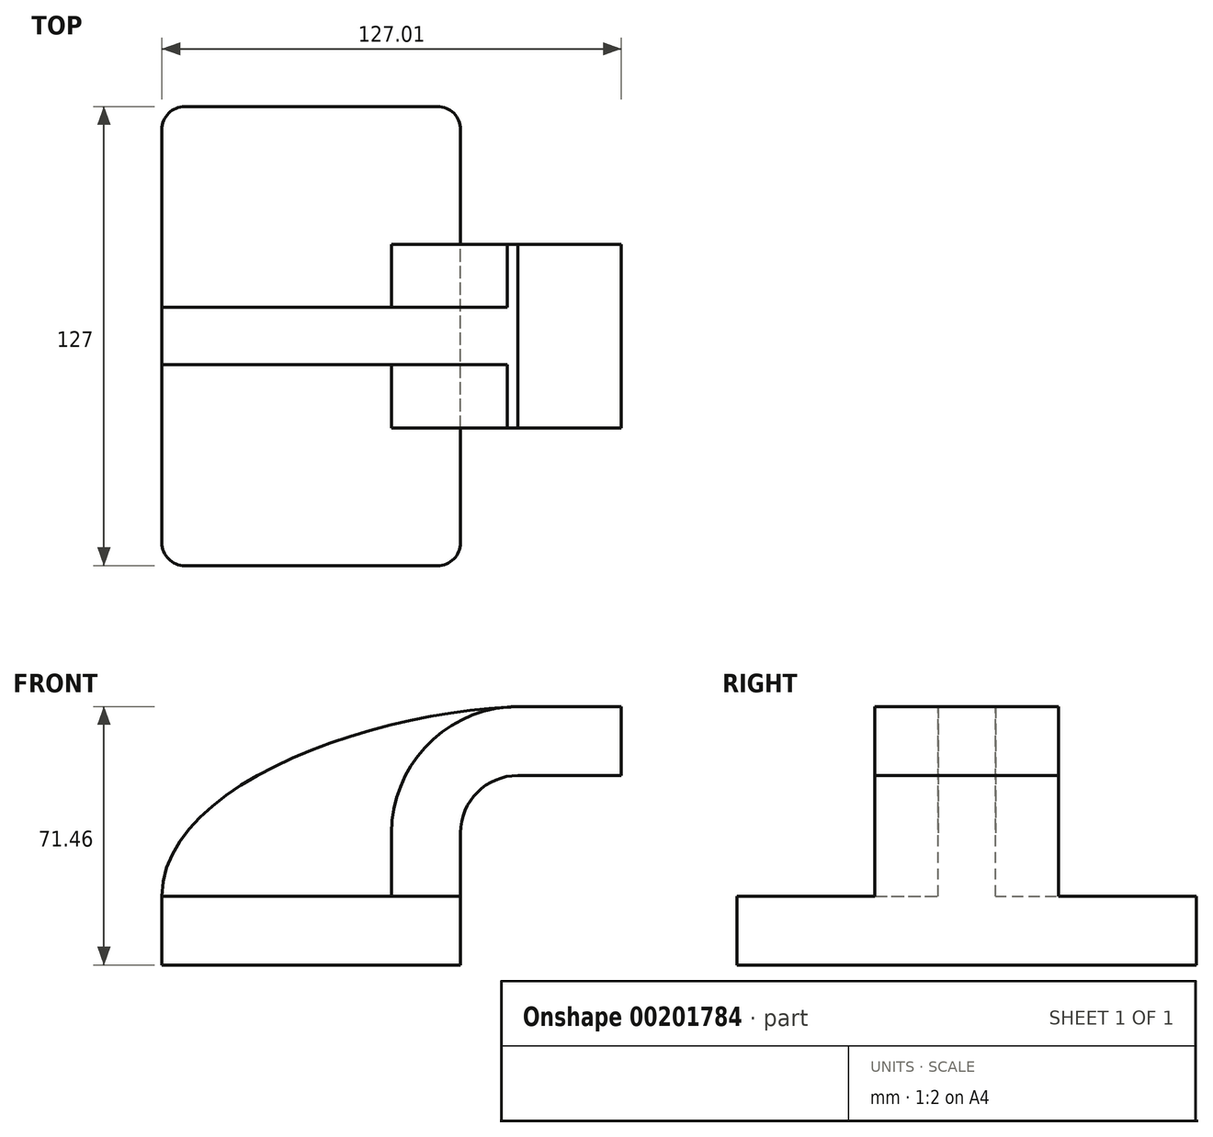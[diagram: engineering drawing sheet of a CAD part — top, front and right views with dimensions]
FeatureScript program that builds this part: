
annotation { "Feature Type Name" : "Feature", "Feature Type Description" : "" }
export const myFeature = defineFeature(function(context is Context, id is Id, definition is map)
    precondition{}
    {
        {
            var Q0;
            Q0=qCreatedBy(makeId("Front.planeOp"),FACE);
            var sketch = newSketch(context, id + "F0", { "sketchPlane" : qUnion([Q0])});
            skLineSegment(sketch, "E0.bottom", {"start": v(41.27, 9.53) * mm, "end": v(-41.28, 9.53) * mm});
            skLineSegment(sketch, "E0.top", {"start": v(41.28, -9.52) * mm, "end": v(-41.27, -9.52) * mm});
            skLineSegment(sketch, "E0.left", {"start": v(41.28, 9.53) * mm, "end": v(41.28, -9.52) * mm});
            skLineSegment(sketch, "E0.right", {"start": v(-41.28, 9.53) * mm, "end": v(-41.28, -9.52) * mm});
            skPoint(sketch, "E0.middle", {"position": v(0, 0) * mm});
            skLineSegment(sketch, "E1.bottom", {"start": v(60.32, 66.68) * mm, "end": v(111.12, 66.68) * mm});
            skLineSegment(sketch, "E1.top", {"start": v(60.32, 38.1) * mm, "end": v(111.12, 38.1) * mm});
            skLineSegment(sketch, "E1.left", {"start": v(60.32, 66.68) * mm, "end": v(60.32, 38.1) * mm});
            skLineSegment(sketch, "E1.right", {"start": v(111.12, 66.68) * mm, "end": v(111.12, 38.1) * mm});
            skPoint(sketch, "E1.middle", {"position": v(85.72, 52.39) * mm});
            skLineSegment(sketch, "E2", {"start": v(41.27, 9.53) * mm, "end": v(41.27, 27) * mm});
            skArc(sketch, "E3", {"start": v(41.27, 27) * mm, "mid": v(45.92, 38.23) * mm, "end": v(57.15, 42.88) * mm});
            skLineSegment(sketch, "E4", {"start": v(57.15, 42.88) * mm, "end": v(88.93, 42.88) * mm});
            skLineSegment(sketch, "E5.0", {"start": v(57.15, 61.93) * mm, "end": v(88.93, 61.93) * mm});
            skArc(sketch, "E5.1", {"start": v(22.22, 27) * mm, "mid": v(32.45, 51.7) * mm, "end": v(57.15, 61.93) * mm});
            skLineSegment(sketch, "E5.2", {"start": v(22.22, 9.53) * mm, "end": v(22.22, 27) * mm});
            skLineSegment(sketch, "E6", {"start": v(85.72, 38.1) * mm, "end": v(85.72, 66.68) * mm});
            skFitSpline(sketch, "E7", {"points": [v(-41.28, 9.52) * mm, v(57.15, 61.93) * mm], "startDerivative": vector(0.69, 95.3) * mm, "endDerivative": vector(114.03, 3.47) * mm});
            skSolve(sketch);
        }
        {
            var Q0;
            Q0=makeQuery(id+"F0.imprint","IMPRINT",FACE,{"disambiguationData":[TD([[makeQuery(id+"F0.imprint","IMPRINT",EDGE,{"derivedFrom":sQuery(id+"F0.wireOp",EDGE,"E0.top")}),-1.0]])]});
            extrude(context, id + "F1", {"entities" : qUnion([Q0]), "endBound" : BoundingType.SYMMETRIC, "depth" : 127 * mm});
        }
        {
            var Q0;
            {var subQ7=sQuery(id+"F0.wireOp",EDGE,"E2");Q0=makeQuery(id+"F0.imprint","IMPRINT",FACE,{"disambiguationData":[TD([[makeQuery(id+"F0.imprint","IMPRINT",EDGE,{"derivedFrom":subQ7}),1.0]])]});}
            var Q1;
            {var subQ0=sQuery(id+"F0.wireOp",EDGE,"E5.0");var subQ1=sQuery(id+"F0.wireOp",EDGE,"E1.left");var subQ2=makeQuery(id+"F0.imprint","INTERSECT",VERTEX,{"derivedFrom":[subQ1,subQ0]});Q1=makeQuery(id+"F0.imprint","IMPRINT",FACE,{"disambiguationData":[TD([[makeQuery(id+"F0.imprint","IMPRINT",EDGE,{"disambiguationData":[TD([[subQ2,-1.0]])],"derivedFrom":subQ1}),1.0]])]});}
            extrude(context, id + "F2", {"entities" : qUnion([Q0, Q1]), "operationType" : NewBodyOperationType.ADD, "endBound" : BoundingType.SYMMETRIC, "depth" : 50.8 * mm});
        }
        {
            var Q0;
            {var subQ3=sQuery(id+"F0.wireOp",EDGE,"E5.2");Q0=makeQuery(id+"F0.imprint","IMPRINT",FACE,{"disambiguationData":[TD([[makeQuery(id+"F0.imprint","IMPRINT",EDGE,{"derivedFrom":subQ3}),1.0]])]});}
            extrude(context, id + "F3", {"entities" : qUnion([Q0]), "operationType" : NewBodyOperationType.ADD, "endBound" : BoundingType.SYMMETRIC, "depth" : 15.88 * mm});
        }
        {
            var Q0;
            Q0=makeQuery(id+"F1.opExtrude","CAP_EDGE",EDGE,{"disambiguationData":[OSD([sQuery(id+"F0.wireOp",EDGE,"E0.left")])],"isStart":false});
            var Q1;
            Q1=makeQuery(id+"F1.opExtrude","CAP_EDGE",EDGE,{"disambiguationData":[OSD([sQuery(id+"F0.wireOp",EDGE,"E0.right")])],"isStart":false});
            var Q2;
            Q2=makeQuery(id+"F1.opExtrude","CAP_EDGE",EDGE,{"disambiguationData":[OSD([sQuery(id+"F0.wireOp",EDGE,"E0.right")])],"isStart":true});
            var Q3;
            Q3=makeQuery(id+"F1.opExtrude","CAP_EDGE",EDGE,{"disambiguationData":[OSD([sQuery(id+"F0.wireOp",EDGE,"E0.left")])],"isStart":true});
            fillet(context, id + "F4", {"entities" : qUnion([Q0, Q1, Q2, Q3]), "radius" : 6.35 * mm, "tangentPropagation" : true, "allowEdgeOverflow" : false});
        }
    });
